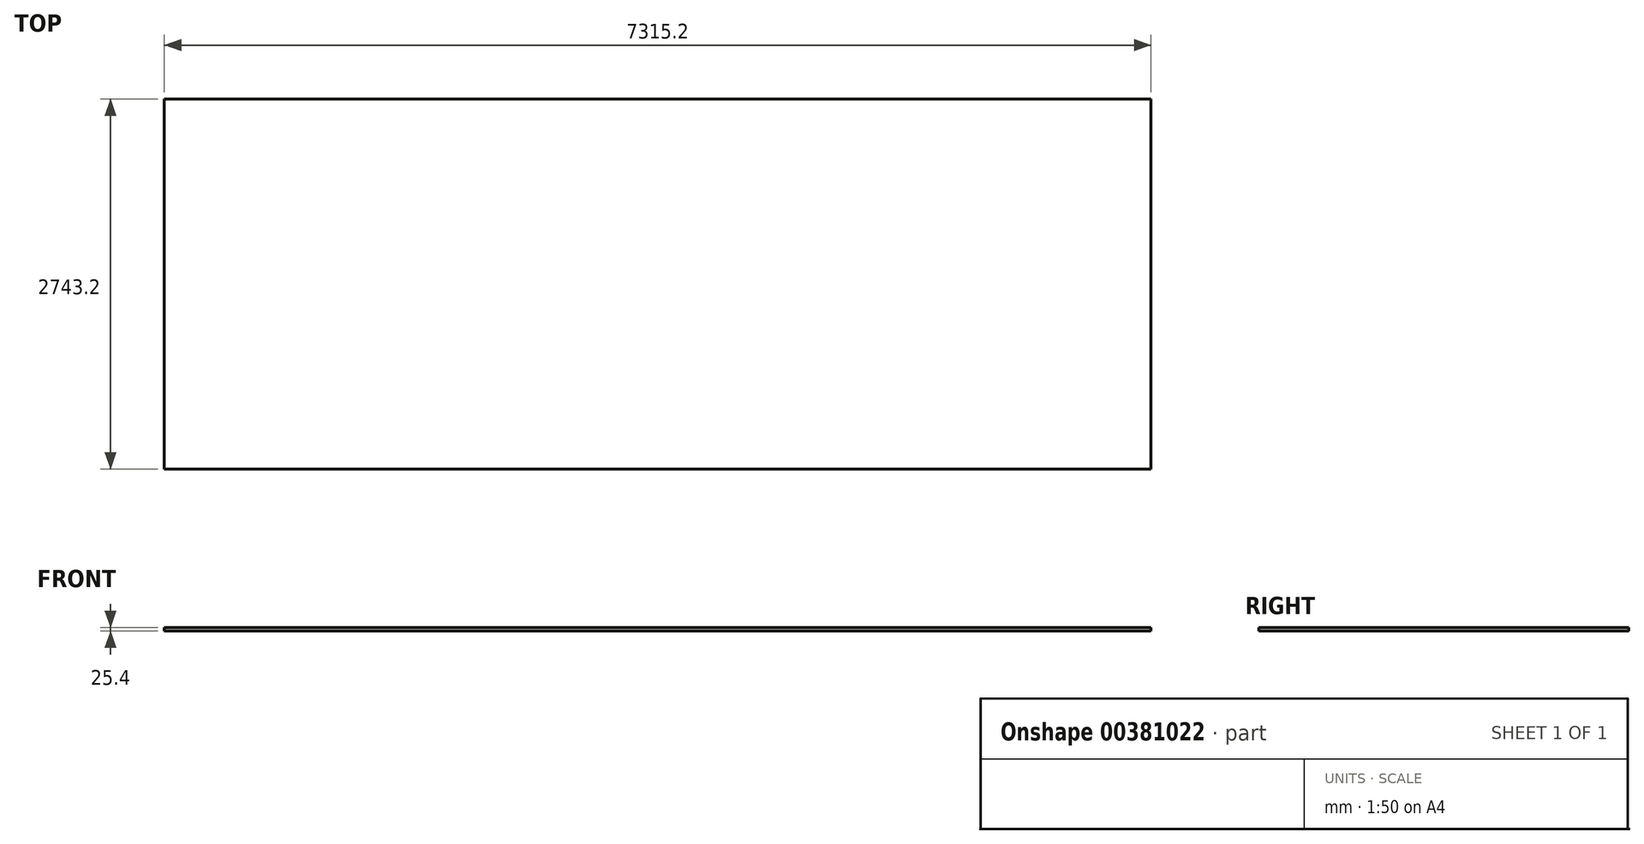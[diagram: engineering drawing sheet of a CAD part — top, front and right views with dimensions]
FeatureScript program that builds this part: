
annotation { "Feature Type Name" : "Feature", "Feature Type Description" : "" }
export const myFeature = defineFeature(function(context is Context, id is Id, definition is map)
    precondition{}
    {
        {
            var Q0;
            Q0=qCreatedBy(makeId("Top.planeOp"),FACE);
            var sketch = newSketch(context, id + "F0", { "sketchPlane" : qUnion([Q0])});
            skLineSegment(sketch, "E0.bottom", {"start": v(3657.6, 1371.6) * mm, "end": v(-3657.6, 1371.6) * mm});
            skLineSegment(sketch, "E0.top", {"start": v(3657.6, -1371.6) * mm, "end": v(-3657.6, -1371.6) * mm});
            skLineSegment(sketch, "E0.left", {"start": v(3657.6, 1371.6) * mm, "end": v(3657.6, -1371.6) * mm});
            skLineSegment(sketch, "E0.right", {"start": v(-3657.6, 1371.6) * mm, "end": v(-3657.6, -1371.6) * mm});
            skPoint(sketch, "E0.middle", {"position": v(0, 0) * mm});
            skSolve(sketch);
        }
        {
            var Q0;
            Q0 = qSketchRegion(id + "F0", true);
            extrude(context, id + "F1", {"entities" : qUnion([Q0]), "depth" : 25.4 * mm});
        }
    });
